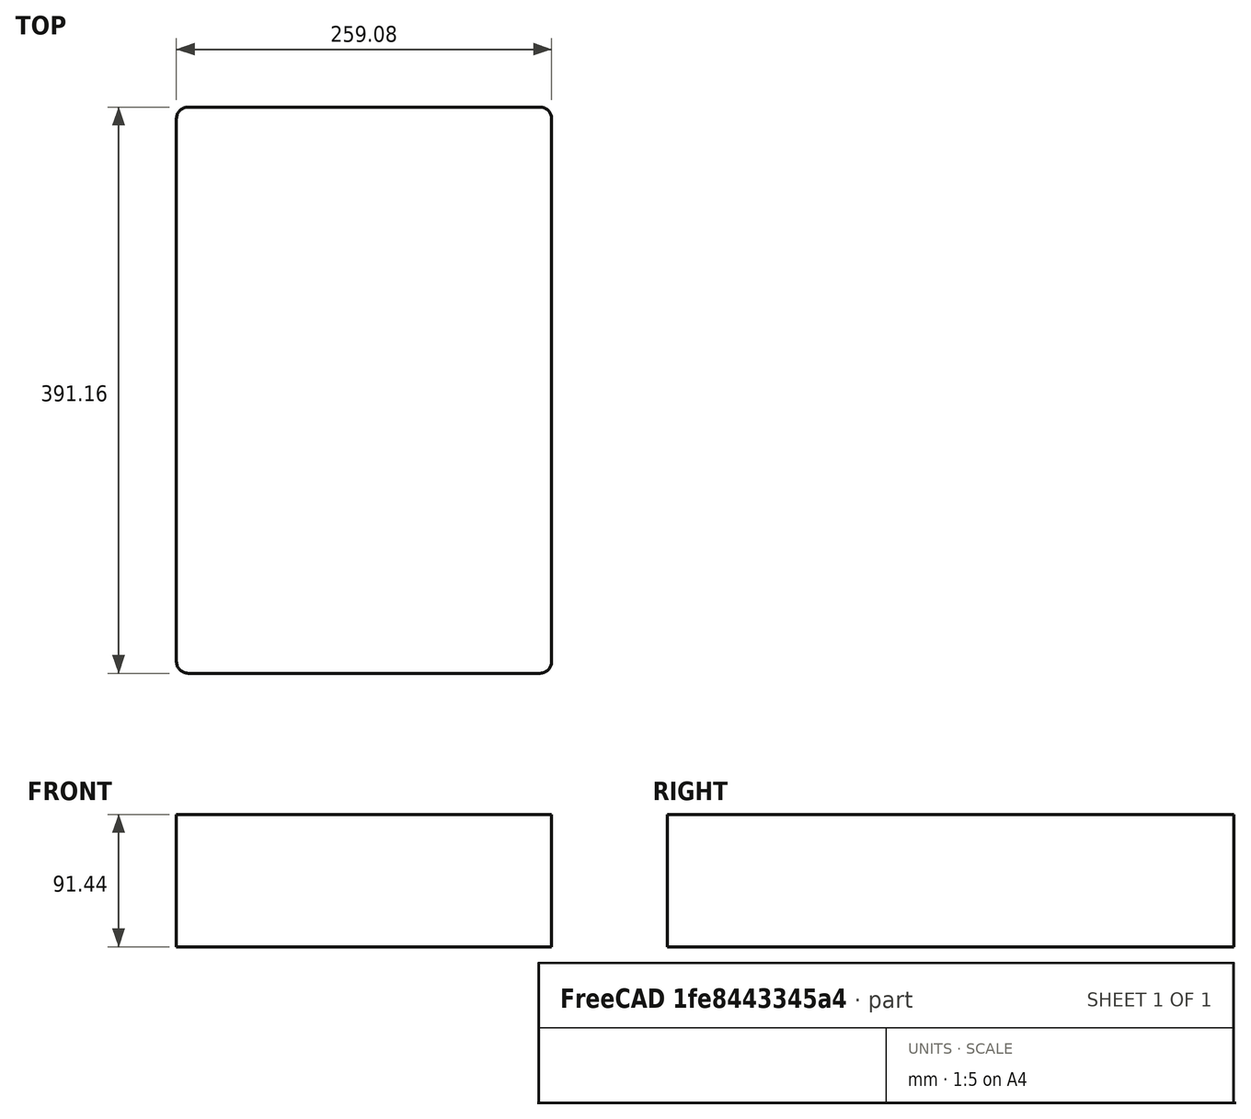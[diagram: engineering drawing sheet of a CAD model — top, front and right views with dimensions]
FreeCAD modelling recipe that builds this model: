
FCSTD DOCUMENT  (FreeCAD 0.20R29410 (Git))
Label: PlayStation5
License: All rights reserved
LicenseURL: http://en.wikipedia.org/wiki/All_rights_reserved
objects: App::DocumentObjectGroup×3, PartDesign::CoordinateSystem×1, App::FeaturePython×1, Sketcher::SketchObject×1, PartDesign::Pad×1, PartDesign::Body×1, App::Part×1
note: 5 computed .brp shape members not serialized (recipe doc carries the construction recipe); baked Part::Feature solids carry a one-line shape summary decoded from their .brp

FEATURE [App::DocumentObjectGroup] Parts
FEATURE [PartDesign::CoordinateSystem] LCS_Origin
  AttacherType = Attacher::AttachEngine3D
  MapMode = 2
  Support = -> [X_Axis]
FEATURE [App::FeaturePython] Variables  # WARN: FeaturePython — macro-defined, semantics opaque (R4)
  Type = App::PropertyContainer
FEATURE [App::DocumentObjectGroup] Constraints
FEATURE [App::DocumentObjectGroup] Configurations
FEATURE [Sketcher::SketchObject] Sketch
  FullyConstrained = true
  MapMode = 5
  Support = -> [XY_Plane001]
  sketch-geometry (10):
    g0: ArcOfCircle CenterX=-121.54 CenterY=187.58 CenterZ=0 NormalX=0 NormalY=0 NormalZ=1 AngleXU=0 Radius=8 StartAngle=1.5708 EndAngle=3.14159
    g1: LineSegment StartX=-121.54 StartY=195.58 StartZ=0 EndX=121.54 EndY=195.58 EndZ=0
    g2: ArcOfCircle CenterX=121.54 CenterY=187.58 CenterZ=0 NormalX=0 NormalY=0 NormalZ=1 AngleXU=0 Radius=8 StartAngle=-9e-16 EndAngle=1.5708
    g3: LineSegment StartX=129.54 StartY=187.58 StartZ=0 EndX=129.54 EndY=-187.58 EndZ=0
    g4: ArcOfCircle CenterX=121.54 CenterY=-187.58 CenterZ=0 NormalX=0 NormalY=0 NormalZ=1 AngleXU=0 Radius=8 StartAngle=4.71239 EndAngle=6.28319
    g5: LineSegment StartX=121.54 StartY=-195.58 StartZ=0 EndX=-121.54 EndY=-195.58 EndZ=0
    g6: ArcOfCircle CenterX=-121.54 CenterY=-187.58 CenterZ=0 NormalX=0 NormalY=0 NormalZ=1 AngleXU=0 Radius=8 StartAngle=3.14159 EndAngle=4.71239
    g7: LineSegment StartX=-129.54 StartY=-187.58 StartZ=0 EndX=-129.54 EndY=187.58 EndZ=0
    g8: GeomPoint X=-129.54 Y=195.58 Z=0
    g9: GeomPoint X=129.54 Y=-195.58 Z=0
  constraints (23):
    c: Tangent(g0,g1) = 1.5708
    c: Tangent(g1,g2) = 1.5708
    c: Tangent(g2,g3) = 1.5708
    c: Tangent(g3,g4) = 1.5708
    c: Tangent(g4,g5) = 1.5708
    c: Tangent(g5,g6) = 1.5708
    c: Tangent(g6,g7) = 1.5708
    c: Tangent(g7,g0) = 1.5708
    c: Horizontal(g1)
    c: Horizontal(g5)
    c: Vertical(g3)
    c: Vertical(g7)
    c: Equal(g0,g2)
    c: Equal(g2,g4)
    c: Equal(g4,g6)
    c: PointOnObject(g8,g1)
    c: PointOnObject(g8,g7)
    c: PointOnObject(g9,g3)
    c: PointOnObject(g9,g5)
    c: Symmetric(g4,g0,g-1)
    c: Radius(g2) = 8
    c: DistanceX(g6,g3) = 259.08
    c: DistanceY(g4,g1) = 391.16
FEATURE [PartDesign::Pad] Pad
  Direction = (0,0,1)
  Length = 91.44
  Length2 = 10
  Profile = -> Sketch
  ReferenceAxis = -> Sketch [N_Axis]
  Type = 0
FEATURE [PartDesign::Body] Body
  Group = -> [Sketch,Pad]
  Origin = -> Origin001
  Tip = -> Pad
FEATURE [App::Part] Assembly
  AssemblyType = Part::Link
  Group = -> [LCS_Origin,Variables,Constraints,Configurations,Body]
  Origin = -> Origin
  Type = Assembly
